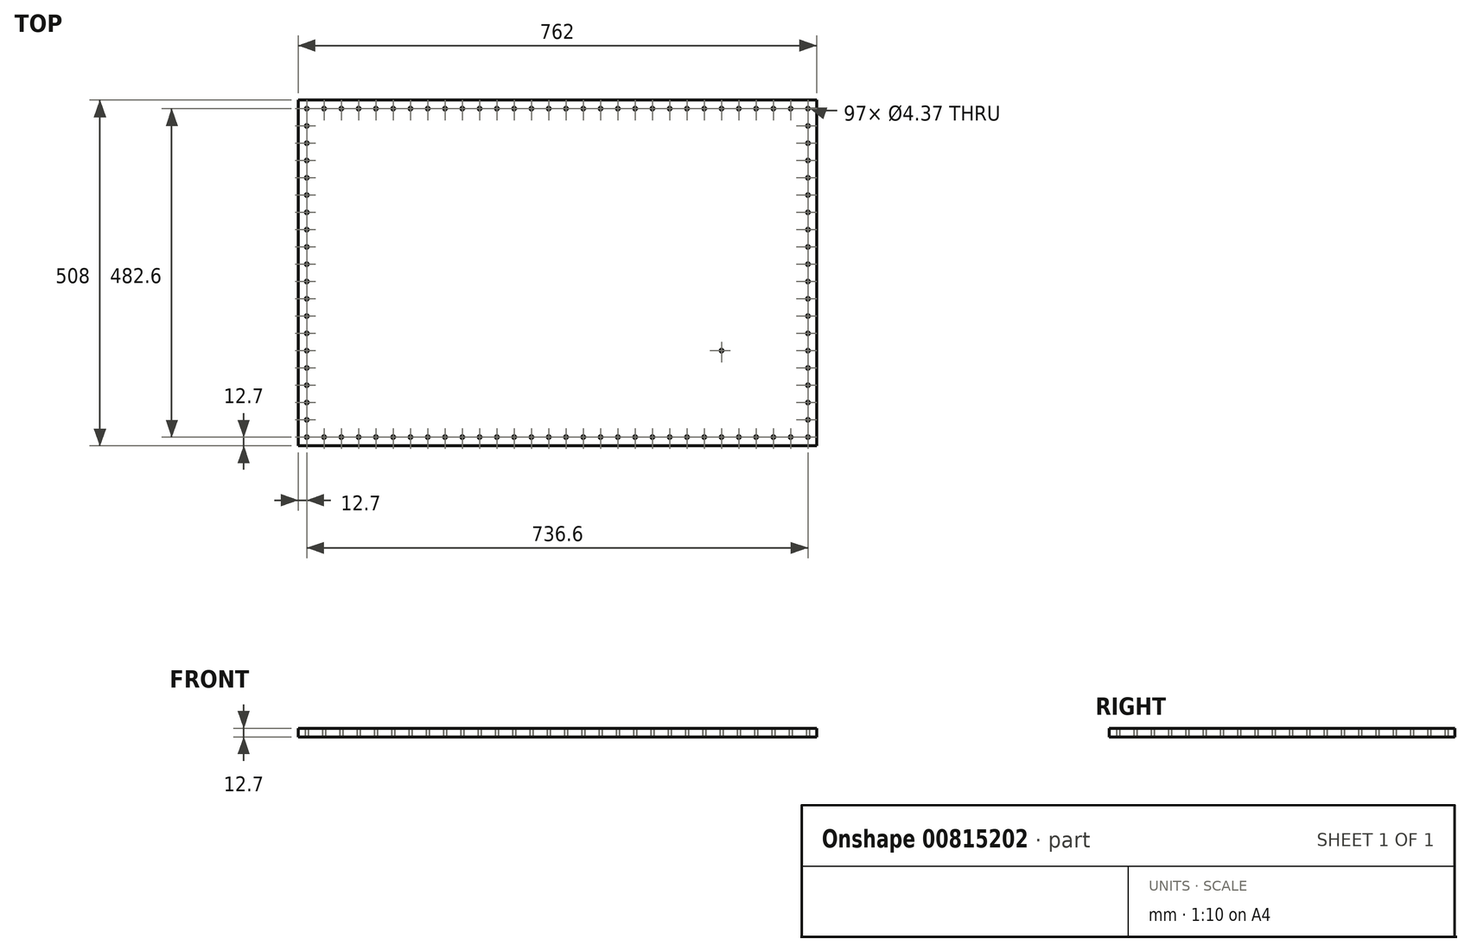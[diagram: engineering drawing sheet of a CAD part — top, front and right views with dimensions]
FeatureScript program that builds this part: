
annotation { "Feature Type Name" : "Feature", "Feature Type Description" : "" }
export const myFeature = defineFeature(function(context is Context, id is Id, definition is map)
    precondition{}
    {
        {
            var Q0;
            Q0=qCreatedBy(makeId("Top.planeOp"),FACE);
            var sketch = newSketch(context, id + "F0", { "sketchPlane" : qUnion([Q0])});
            skLineSegment(sketch, "E0.bottom", {"start": v(0, 0) * mm, "end": v(762, 0) * mm});
            skLineSegment(sketch, "E0.top", {"start": v(0, -508) * mm, "end": v(762, -508) * mm});
            skLineSegment(sketch, "E0.left", {"start": v(0, 0) * mm, "end": v(0, -508) * mm});
            skLineSegment(sketch, "E0.right", {"start": v(762, 0) * mm, "end": v(762, -508) * mm});
            skCircle(sketch, "E1", {"center": v(12.7, -495.3) * mm, "radius": 2.18 * mm});
            skCircle(sketch, "E2.1.0.0", {"center": v(38.1, -495.3) * mm, "radius": 2.18 * mm});
            skCircle(sketch, "E2.2.0.0", {"center": v(63.5, -495.3) * mm, "radius": 2.18 * mm});
            skCircle(sketch, "E2.3.0.0", {"center": v(88.9, -495.3) * mm, "radius": 2.18 * mm});
            skCircle(sketch, "E2.4.0.0", {"center": v(114.3, -495.3) * mm, "radius": 2.18 * mm});
            skCircle(sketch, "E2.5.0.0", {"center": v(139.7, -495.3) * mm, "radius": 2.18 * mm});
            skCircle(sketch, "E2.6.0.0", {"center": v(165.1, -495.3) * mm, "radius": 2.18 * mm});
            skCircle(sketch, "E2.7.0.0", {"center": v(190.5, -495.3) * mm, "radius": 2.18 * mm});
            skCircle(sketch, "E2.8.0.0", {"center": v(215.9, -495.3) * mm, "radius": 2.18 * mm});
            skCircle(sketch, "E2.9.0.0", {"center": v(241.3, -495.3) * mm, "radius": 2.18 * mm});
            skCircle(sketch, "E2.10.0.0", {"center": v(266.7, -495.3) * mm, "radius": 2.18 * mm});
            skCircle(sketch, "E2.11.0.0", {"center": v(292.1, -495.3) * mm, "radius": 2.18 * mm});
            skCircle(sketch, "E2.12.0.0", {"center": v(317.5, -495.3) * mm, "radius": 2.18 * mm});
            skCircle(sketch, "E2.13.0.0", {"center": v(342.9, -495.3) * mm, "radius": 2.18 * mm});
            skCircle(sketch, "E2.14.0.0", {"center": v(368.3, -495.3) * mm, "radius": 2.18 * mm});
            skCircle(sketch, "E2.15.0.0", {"center": v(393.7, -495.3) * mm, "radius": 2.18 * mm});
            skCircle(sketch, "E2.16.0.0", {"center": v(419.1, -495.3) * mm, "radius": 2.18 * mm});
            skCircle(sketch, "E2.17.0.0", {"center": v(444.5, -495.3) * mm, "radius": 2.18 * mm});
            skCircle(sketch, "E2.18.0.0", {"center": v(469.9, -495.3) * mm, "radius": 2.18 * mm});
            skCircle(sketch, "E2.19.0.0", {"center": v(495.3, -495.3) * mm, "radius": 2.18 * mm});
            skCircle(sketch, "E2.20.0.0", {"center": v(520.7, -495.3) * mm, "radius": 2.18 * mm});
            skCircle(sketch, "E2.21.0.0", {"center": v(546.1, -495.3) * mm, "radius": 2.18 * mm});
            skCircle(sketch, "E2.22.0.0", {"center": v(571.5, -495.3) * mm, "radius": 2.18 * mm});
            skCircle(sketch, "E2.23.0.0", {"center": v(596.9, -495.3) * mm, "radius": 2.18 * mm});
            skCircle(sketch, "E2.24.0.0", {"center": v(622.3, -495.3) * mm, "radius": 2.18 * mm});
            skLineSegment(sketch, "E2.direction1", {"start": v(12.7, -495.3) * mm, "end": v(38.1, -495.3) * mm, "construction": true});
            skCircle(sketch, "E3.0.1.0", {"center": v(12.7, -469.9) * mm, "radius": 2.18 * mm});
            skCircle(sketch, "E3.0.2.0", {"center": v(12.7, -444.5) * mm, "radius": 2.18 * mm});
            skCircle(sketch, "E3.0.3.0", {"center": v(12.7, -419.1) * mm, "radius": 2.18 * mm});
            skCircle(sketch, "E3.0.4.0", {"center": v(12.7, -393.7) * mm, "radius": 2.18 * mm});
            skCircle(sketch, "E3.0.5.0", {"center": v(12.7, -368.3) * mm, "radius": 2.18 * mm});
            skCircle(sketch, "E3.0.6.0", {"center": v(12.7, -342.9) * mm, "radius": 2.18 * mm});
            skCircle(sketch, "E3.0.7.0", {"center": v(12.7, -317.5) * mm, "radius": 2.18 * mm});
            skCircle(sketch, "E3.0.8.0", {"center": v(12.7, -292.1) * mm, "radius": 2.18 * mm});
            skCircle(sketch, "E3.0.9.0", {"center": v(12.7, -266.7) * mm, "radius": 2.18 * mm});
            skCircle(sketch, "E3.0.10.0", {"center": v(12.7, -241.3) * mm, "radius": 2.18 * mm});
            skCircle(sketch, "E3.0.11.0", {"center": v(12.7, -215.9) * mm, "radius": 2.18 * mm});
            skLineSegment(sketch, "E3.direction2", {"start": v(12.7, -495.3) * mm, "end": v(12.7, -469.9) * mm, "construction": true});
            skLineSegment(sketch, "E4.direction1", {"start": v(12.7, -215.9) * mm, "end": v(38.1, -215.9) * mm, "construction": true});
            skCircle(sketch, "E5.0.11.0", {"center": v(622.3, -368.3) * mm, "radius": 2.18 * mm});
            skCircle(sketch, "E6.0.0.12", {"center": v(12.7, -190.5) * mm, "radius": 2.18 * mm});
            skCircle(sketch, "E6.0.0.13", {"center": v(12.7, -165.1) * mm, "radius": 2.18 * mm});
            skCircle(sketch, "E6.0.0.14", {"center": v(12.7, -139.7) * mm, "radius": 2.18 * mm});
            skCircle(sketch, "E7.0.25.0", {"center": v(647.7, -495.3) * mm, "radius": 2.18 * mm});
            skCircle(sketch, "E7.0.26.0", {"center": v(673.1, -495.3) * mm, "radius": 2.18 * mm});
            skCircle(sketch, "E7.0.27.0", {"center": v(698.5, -495.3) * mm, "radius": 2.18 * mm});
            skCircle(sketch, "E7.0.28.0", {"center": v(723.9, -495.3) * mm, "radius": 2.18 * mm});
            skCircle(sketch, "E7.0.29.0", {"center": v(749.3, -495.3) * mm, "radius": 2.18 * mm});
            skCircle(sketch, "E8.29.0.0", {"center": v(749.3, -139.7) * mm, "radius": 2.18 * mm});
            skLineSegment(sketch, "E8.direction1", {"start": v(12.7, -139.7) * mm, "end": v(38.1, -139.7) * mm, "construction": true});
            skCircle(sketch, "E9.0.1.0", {"center": v(749.3, -165.1) * mm, "radius": 2.18 * mm});
            skCircle(sketch, "E9.0.2.0", {"center": v(749.3, -190.5) * mm, "radius": 2.18 * mm});
            skCircle(sketch, "E9.0.3.0", {"center": v(749.3, -215.9) * mm, "radius": 2.18 * mm});
            skCircle(sketch, "E9.0.4.0", {"center": v(749.3, -241.3) * mm, "radius": 2.18 * mm});
            skCircle(sketch, "E9.0.5.0", {"center": v(749.3, -266.7) * mm, "radius": 2.18 * mm});
            skCircle(sketch, "E9.0.6.0", {"center": v(749.3, -292.1) * mm, "radius": 2.18 * mm});
            skCircle(sketch, "E9.0.7.0", {"center": v(749.3, -317.5) * mm, "radius": 2.18 * mm});
            skCircle(sketch, "E9.0.8.0", {"center": v(749.3, -342.9) * mm, "radius": 2.18 * mm});
            skCircle(sketch, "E9.0.9.0", {"center": v(749.3, -368.3) * mm, "radius": 2.18 * mm});
            skCircle(sketch, "E9.0.10.0", {"center": v(749.3, -393.7) * mm, "radius": 2.18 * mm});
            skCircle(sketch, "E9.0.11.0", {"center": v(749.3, -419.1) * mm, "radius": 2.18 * mm});
            skCircle(sketch, "E9.0.12.0", {"center": v(749.3, -444.5) * mm, "radius": 2.18 * mm});
            skCircle(sketch, "E9.0.13.0", {"center": v(749.3, -469.9) * mm, "radius": 2.18 * mm});
            skLineSegment(sketch, "E9.direction1", {"start": v(749.3, -139.7) * mm, "end": v(774.7, -139.7) * mm, "construction": true});
            skLineSegment(sketch, "E9.direction2", {"start": v(749.3, -139.7) * mm, "end": v(749.3, -165.1) * mm, "construction": true});
            skCircle(sketch, "E10.0.0.15", {"center": v(12.7, -114.3) * mm, "radius": 2.18 * mm});
            skCircle(sketch, "E10.0.0.16", {"center": v(12.7, -88.9) * mm, "radius": 2.18 * mm});
            skCircle(sketch, "E10.0.0.17", {"center": v(12.7, -63.5) * mm, "radius": 2.18 * mm});
            skCircle(sketch, "E10.0.0.18", {"center": v(12.7, -38.1) * mm, "radius": 2.18 * mm});
            skCircle(sketch, "E10.0.0.19", {"center": v(12.7, -12.7) * mm, "radius": 2.18 * mm});
            skCircle(sketch, "E11.0.1.0", {"center": v(749.3, -114.3) * mm, "radius": 2.18 * mm});
            skCircle(sketch, "E11.0.2.0", {"center": v(749.3, -88.9) * mm, "radius": 2.18 * mm});
            skCircle(sketch, "E11.0.3.0", {"center": v(749.3, -63.5) * mm, "radius": 2.18 * mm});
            skCircle(sketch, "E11.0.4.0", {"center": v(749.3, -38.1) * mm, "radius": 2.18 * mm});
            skCircle(sketch, "E11.0.5.0", {"center": v(749.3, -12.7) * mm, "radius": 2.18 * mm});
            skLineSegment(sketch, "E11.direction2", {"start": v(749.3, -139.7) * mm, "end": v(749.3, -114.3) * mm, "construction": true});
            skCircle(sketch, "E12.1.0.0", {"center": v(723.9, -12.7) * mm, "radius": 2.18 * mm});
            skCircle(sketch, "E12.2.0.0", {"center": v(698.5, -12.7) * mm, "radius": 2.18 * mm});
            skCircle(sketch, "E12.3.0.0", {"center": v(673.1, -12.7) * mm, "radius": 2.18 * mm});
            skCircle(sketch, "E12.4.0.0", {"center": v(647.7, -12.7) * mm, "radius": 2.18 * mm});
            skCircle(sketch, "E12.5.0.0", {"center": v(622.3, -12.7) * mm, "radius": 2.18 * mm});
            skCircle(sketch, "E12.6.0.0", {"center": v(596.9, -12.7) * mm, "radius": 2.18 * mm});
            skCircle(sketch, "E12.7.0.0", {"center": v(571.5, -12.7) * mm, "radius": 2.18 * mm});
            skCircle(sketch, "E12.8.0.0", {"center": v(546.1, -12.7) * mm, "radius": 2.18 * mm});
            skCircle(sketch, "E12.9.0.0", {"center": v(520.7, -12.7) * mm, "radius": 2.18 * mm});
            skCircle(sketch, "E12.10.0.0", {"center": v(495.3, -12.7) * mm, "radius": 2.18 * mm});
            skCircle(sketch, "E12.11.0.0", {"center": v(469.9, -12.7) * mm, "radius": 2.18 * mm});
            skCircle(sketch, "E12.12.0.0", {"center": v(444.5, -12.7) * mm, "radius": 2.18 * mm});
            skCircle(sketch, "E12.13.0.0", {"center": v(419.1, -12.7) * mm, "radius": 2.18 * mm});
            skCircle(sketch, "E12.14.0.0", {"center": v(393.7, -12.7) * mm, "radius": 2.18 * mm});
            skCircle(sketch, "E12.15.0.0", {"center": v(368.3, -12.7) * mm, "radius": 2.18 * mm});
            skCircle(sketch, "E12.16.0.0", {"center": v(342.9, -12.7) * mm, "radius": 2.18 * mm});
            skCircle(sketch, "E12.17.0.0", {"center": v(317.5, -12.7) * mm, "radius": 2.18 * mm});
            skCircle(sketch, "E12.18.0.0", {"center": v(292.1, -12.7) * mm, "radius": 2.18 * mm});
            skCircle(sketch, "E12.19.0.0", {"center": v(266.7, -12.7) * mm, "radius": 2.18 * mm});
            skCircle(sketch, "E12.20.0.0", {"center": v(241.3, -12.7) * mm, "radius": 2.18 * mm});
            skCircle(sketch, "E12.21.0.0", {"center": v(215.9, -12.7) * mm, "radius": 2.18 * mm});
            skCircle(sketch, "E12.22.0.0", {"center": v(190.5, -12.7) * mm, "radius": 2.18 * mm});
            skCircle(sketch, "E12.23.0.0", {"center": v(165.1, -12.7) * mm, "radius": 2.18 * mm});
            skCircle(sketch, "E12.24.0.0", {"center": v(139.7, -12.7) * mm, "radius": 2.18 * mm});
            skCircle(sketch, "E12.25.0.0", {"center": v(114.3, -12.7) * mm, "radius": 2.18 * mm});
            skCircle(sketch, "E12.26.0.0", {"center": v(88.9, -12.7) * mm, "radius": 2.18 * mm});
            skCircle(sketch, "E12.27.0.0", {"center": v(63.5, -12.7) * mm, "radius": 2.18 * mm});
            skCircle(sketch, "E12.28.0.0", {"center": v(38.1, -12.7) * mm, "radius": 2.18 * mm});
            skLineSegment(sketch, "E12.direction1", {"start": v(749.3, -12.7) * mm, "end": v(723.9, -12.7) * mm, "construction": true});
            skSolve(sketch);
        }
        {
            var Q0;
            Q0=makeQuery(id+"F0.imprint","IMPRINT",FACE,{"disambiguationData":[TD([[makeQuery(id+"F0.imprint","IMPRINT",EDGE,{"derivedFrom":sQuery(id+"F0.wireOp",EDGE,"E0.bottom")}),-1.0]])]});
            extrude(context, id + "F1", {"entities" : qUnion([Q0]), "depth" : 12.7 * mm, "offsetDistance" : 25.4 * mm});
        }
    });
